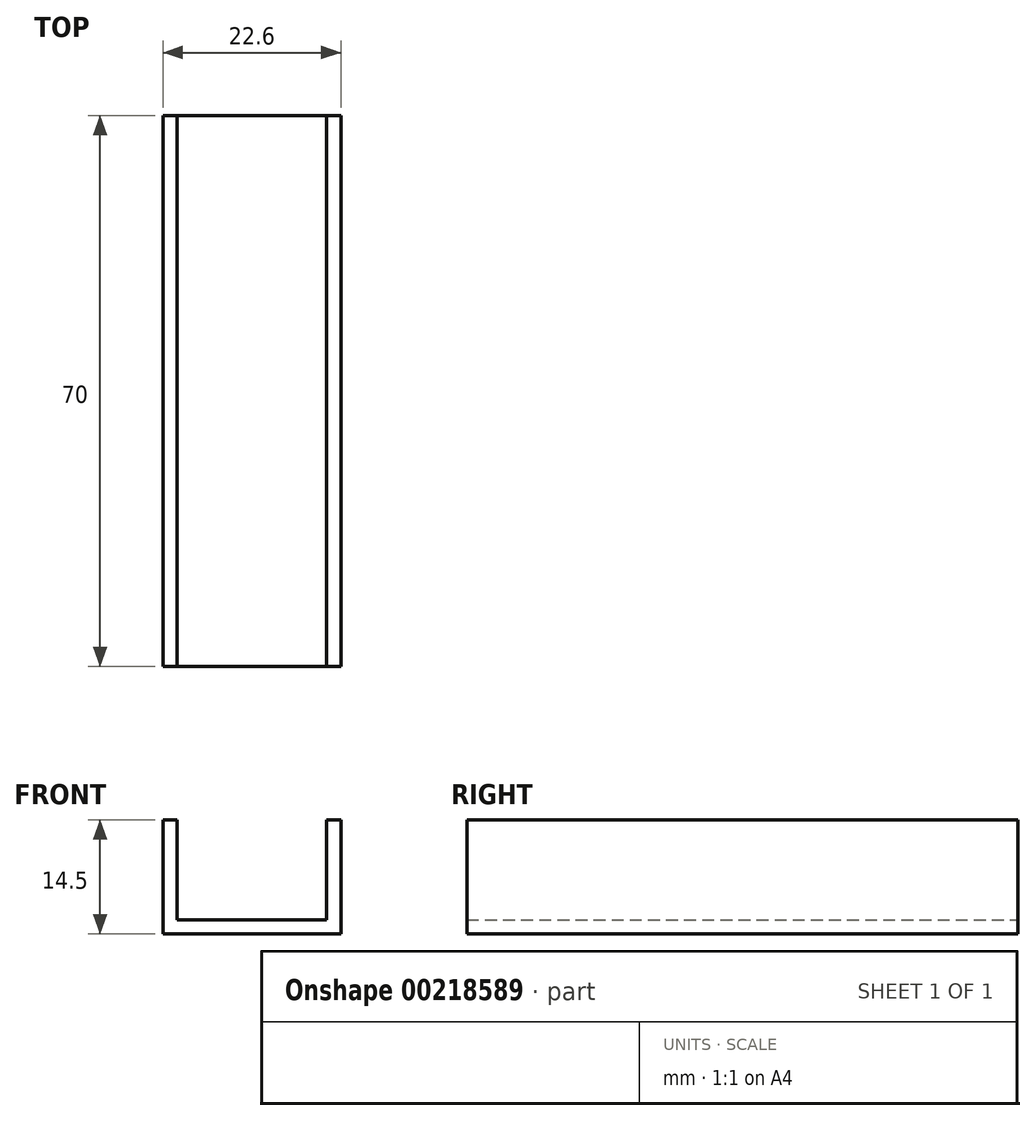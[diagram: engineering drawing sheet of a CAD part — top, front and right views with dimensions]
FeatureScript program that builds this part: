
annotation { "Feature Type Name" : "Feature", "Feature Type Description" : "" }
export const myFeature = defineFeature(function(context is Context, id is Id, definition is map)
    precondition{}
    {
        {
            var Q0;
            Q0=qCreatedBy(makeId("Front.planeOp"),FACE);
            var sketch = newSketch(context, id + "F0", { "sketchPlane" : qUnion([Q0])});
            skLineSegment(sketch, "E0", {"start": v(-55.35, 16.16) * mm, "end": v(-32.75, 16.16) * mm});
            skLineSegment(sketch, "E1", {"start": v(-32.75, 16.16) * mm, "end": v(-32.75, 30.66) * mm});
            skLineSegment(sketch, "E2", {"start": v(-32.75, 30.66) * mm, "end": v(-34.55, 30.66) * mm});
            skLineSegment(sketch, "E3", {"start": v(-34.55, 30.66) * mm, "end": v(-34.55, 17.96) * mm});
            skLineSegment(sketch, "E4", {"start": v(-34.55, 17.96) * mm, "end": v(-53.55, 17.96) * mm});
            skLineSegment(sketch, "E5", {"start": v(-53.55, 17.96) * mm, "end": v(-53.55, 30.66) * mm});
            skLineSegment(sketch, "E6", {"start": v(-53.55, 30.66) * mm, "end": v(-55.35, 30.66) * mm});
            skLineSegment(sketch, "E7", {"start": v(-55.35, 30.66) * mm, "end": v(-55.35, 16.16) * mm});
            skLineSegment(sketch, "E8", {"start": v(-53.55, 17.96) * mm, "end": v(-53.55, 16.16) * mm, "construction": true});
            skSolve(sketch);
        }
        {
            var Q0;
            Q0 = qSketchRegion(id + "F0", true);
            extrude(context, id + "F1", {"entities" : qUnion([Q0]), "depth" : 70 * mm, "offsetDistance" : 25 * mm});
        }
    });
